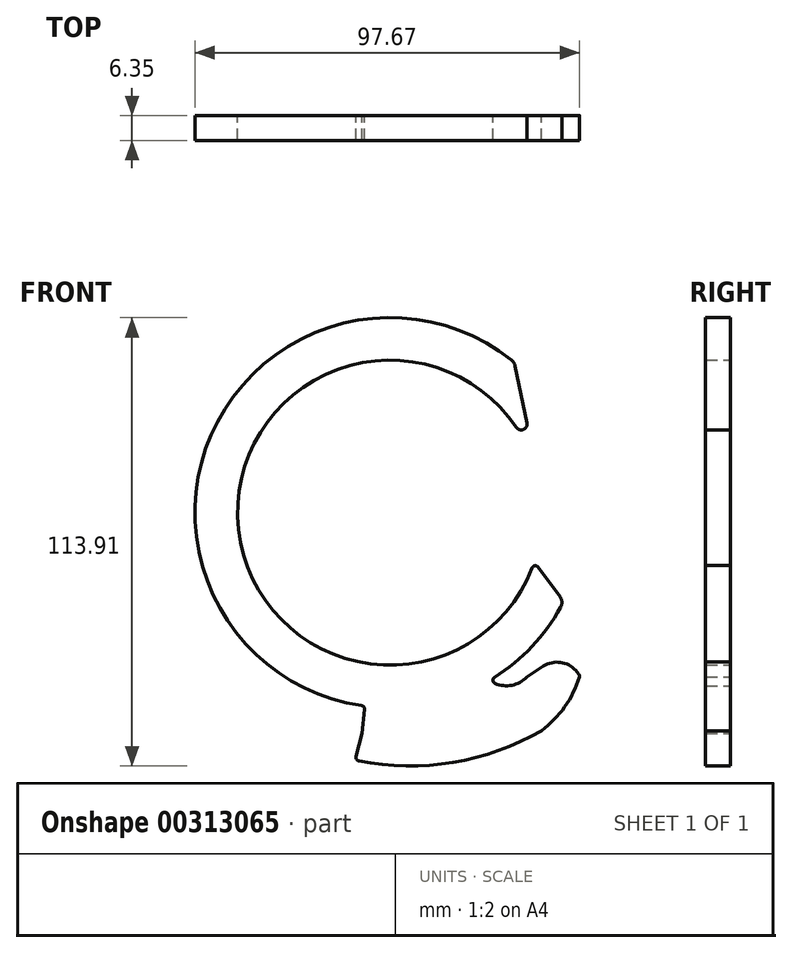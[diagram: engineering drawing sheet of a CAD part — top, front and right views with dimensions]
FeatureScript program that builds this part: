
annotation { "Feature Type Name" : "Feature", "Feature Type Description" : "" }
export const myFeature = defineFeature(function(context is Context, id is Id, definition is map)
    precondition{}
    {
        {
            var Q0;
            Q0=qCreatedBy(makeId("Front.planeOp"),FACE);
            var sketch = newSketch(context, id + "F0", { "sketchPlane" : qUnion([Q0])});
            skArc(sketch, "E0", {"start": v(32.1, 21.67) * mm, "mid": v(-38.5, -4.31) * mm, "end": v(36.1, -14.03) * mm});
            skLineSegment(sketch, "E1", {"start": v(47.9, -40.95) * mm, "end": v(47.18, -40.12) * mm});
            skLineSegment(sketch, "E2", {"start": v(-8.62, -61.99) * mm, "end": v(-7.07, -56.1) * mm});
            skLineSegment(sketch, "E3", {"start": v(-7.07, -56.1) * mm, "end": v(-6.48, -49.97) * mm});
            skArc(sketch, "E4", {"start": v(38.5, -55.4) * mm, "mid": v(44.37, -49.35) * mm, "end": v(48.09, -41.78) * mm});
            skArc(sketch, "E5", {"start": v(-7.94, -63.07) * mm, "mid": v(15.97, -63.46) * mm, "end": v(38.5, -55.4) * mm});
            skArc(sketch, "E6", {"start": v(26.56, -41.83) * mm, "mid": v(36.06, -33.99) * mm, "end": v(43.33, -24.04) * mm});
            skArc(sketch, "E7", {"start": v(26.67, -43.37) * mm, "mid": v(30.97, -43.85) * mm, "end": v(34.74, -41.72) * mm});
            skLineSegment(sketch, "E8", {"start": v(34.74, -41.72) * mm, "end": v(39, -38.99) * mm});
            skPoint(sketch, "E9.center.orphan", {"position": v(25.15, -29.9) * mm});
            skPoint(sketch, "E10.start.orphan", {"position": v(34.7, -29.9) * mm});
            skPoint(sketch, "E11.end.orphan", {"position": v(49.55, 0) * mm});
            skPoint(sketch, "E12.visualSharp", {"position": v(43.57, -36.05) * mm});
            skArc(sketch, "E12.filletArc", {"start": v(47.18, -40.12) * mm, "mid": v(43.3, -38.04) * mm, "end": v(39, -38.99) * mm});
            skPoint(sketch, "E13.visualSharp", {"position": v(-8.85, -62.88) * mm});
            skArc(sketch, "E13.filletArc", {"start": v(-8.62, -61.99) * mm, "mid": v(-8.51, -62.67) * mm, "end": v(-7.94, -63.07) * mm});
            skPoint(sketch, "E14.visualSharp", {"position": v(48.23, -41.3) * mm});
            skArc(sketch, "E14.filletArc", {"start": v(48.09, -41.78) * mm, "mid": v(48.1, -41.34) * mm, "end": v(47.9, -40.95) * mm});
            skPoint(sketch, "E15.visualSharp", {"position": v(25.33, -42.59) * mm});
            skArc(sketch, "E15.filletArc", {"start": v(26.56, -41.83) * mm, "mid": v(26.15, -42.64) * mm, "end": v(26.67, -43.37) * mm});
            skPoint(sketch, "E16.visualSharp", {"position": v(-6.4, -49.14) * mm});
            skArc(sketch, "E16.filletArc", {"start": v(-6.48, -49.97) * mm, "mid": v(-6.66, -49.35) * mm, "end": v(-7.22, -49.02) * mm});
            skLineSegment(sketch, "E17", {"start": v(34.8, 22.8) * mm, "end": v(31.76, 37.3) * mm});
            skArc(sketch, "E18.trimOffspring", {"start": v(30.86, 38.77) * mm, "mid": v(-45.46, 19.72) * mm, "end": v(-7.22, -49.02) * mm});
            skPoint(sketch, "E19.visualSharp", {"position": v(44.25, -22.3) * mm});
            skArc(sketch, "E19.filletArc", {"start": v(44.1, -22.58) * mm, "mid": v(44.2, -22.3) * mm, "end": v(44.18, -22) * mm});
            skLineSegment(sketch, "E20", {"start": v(43.15, -21.3) * mm, "end": v(37.62, -13.82) * mm});
            skPoint(sketch, "E21.visualSharp", {"position": v(36.66, -12.52) * mm});
            skArc(sketch, "E21.filletArc", {"start": v(37.62, -13.82) * mm, "mid": v(36.8, -13.48) * mm, "end": v(36.1, -14.03) * mm});
            skPoint(sketch, "E22.visualSharp", {"position": v(44.1, -22.58) * mm});
            skArc(sketch, "E22.filletArc", {"start": v(43.33, -24.04) * mm, "mid": v(43.64, -22.64) * mm, "end": v(43.15, -21.3) * mm});
            skPoint(sketch, "E23.visualSharp", {"position": v(37.91, 7.94) * mm});
            skArc(sketch, "E23.filletArc", {"start": v(32.1, 21.67) * mm, "mid": v(33.92, 21.13) * mm, "end": v(34.8, 22.8) * mm});
            skPoint(sketch, "E24.visualSharp", {"position": v(31.58, 38.19) * mm});
            skArc(sketch, "E24.filletArc", {"start": v(31.76, 37.3) * mm, "mid": v(31.44, 38.11) * mm, "end": v(30.86, 38.77) * mm});
            skSolve(sketch);
        }
        {
            var Q0;
            Q0 = qSketchRegion(id + "F0", true);
            extrude(context, id + "F1", {"entities" : qUnion([Q0]), "depth" : 6.35 * mm});
        }
    });
